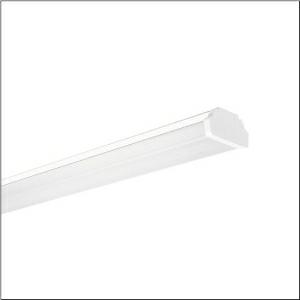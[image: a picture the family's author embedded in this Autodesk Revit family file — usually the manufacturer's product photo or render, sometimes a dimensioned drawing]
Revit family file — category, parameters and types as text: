
# Revit family: dus_r__31_gen_2_53bd813dv4dxd2_23c6
name_source: partatom
category: Lighting Fixtures
units: mm (PartAtom-declared; Revit-internal decimal feet)

## family parameters
Cut with Voids When Loaded = No
Host = Face
Light Source = No
Part Type = Normal
Room Calculation Point = No
Round Connector Dimension = Use Diameter
Shared = No

## types (1)
- --- (1 x LED, 13370 lm, 74.9 W, 4000K)
    Apparent Load = 75 VA
    CIE Flux Codes = 62 83 95 93 100
    Color Rendering = 80
    Color Temperature = 4000K
    Default Elevation = 1800 mm
    Description = DUS® 31 Gen.2, luminaire insert, of sheet steel, coil coated, white, length: 1.535mm, width: 81mm, height: 90mm, 5x system unit, system units: 307mm, LED rated luminous flux: 13.370lm, light colour: 840, control gear: DALI 2, control gear: ECG DALI, with plug, 5-pole, with phase selection, mains connection: 220..240V, AC, 50/60Hz, rated input power: 75W, through-wiring accessed according to module size, primary optical cover: cover, of PMMA, light emission: direct distribution, primary light characteristic: symmetric, protection rating (complete): IP20, protection rating (LED compartment): IP50, insulation class (complete): insulation class I (protective earthing), certification: CE, ENEC, VDE, UKCA, impact resistance: IK03, permissible ambient temperature for indoor applications: -25..+35°C, corresponds to IFS (International Featured Standards) requirements for safety and quality in the food industry, reducing of maximum allowable ambient temperature of 5°C with ceiling mounting, packaging unit: 1 piece
    Height = 95 mm
    Lamp = 1 x LED
    Lamp Light Flux = 13370 lm
    Lamp Power = 74.9 W
    Lamp count = 1
    Length = 1535 mm
    Luminous efficacy = 179 lm/W
    Manufacturer = Siteco
    ModVariant = No
    Model = 53BD813DV4DXD2
    Mounting Place = Ceiling
    Mounting Type = Pendant
    Number of Poles = 1
    OnlyDefault = Yes
    Power Factor = 1
    Product Name = DUS® 31 Gen.2
    Product group = luminaire insert
    ProductGroupID = 902
    Protection Class = Protection class I
    Protection Degree = IP 20
    RLX_Detail_Level = 1
    RLX_Emergency_Light_Flux = 0 lm
    RLX_Emergency_Type = 0
    RLX_Emergency_Type_DB = No
    RlxData = <blob elided: 32261 chars, md5=8da05df9>
    Socket = socket
    Standby Power = 0 W
    System Light Flux = 13370 lm
    System Power = 75 W
    Type Comments = factory setting: luminous flux: 100 % | dim-lin: 254 | 511 mA
    Type Image = l_1319596.jpg
    URL = http://relux.com
    VarID = @adj_042874
    Voltage = 0 V
    Weight = 0.00 kg
    Width = 81 mm

## geometry (parser evidence)
native form markers: Blend x4, Sweep x12
no freeform markers — native parametric forms only
